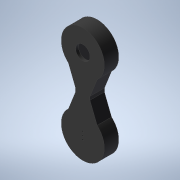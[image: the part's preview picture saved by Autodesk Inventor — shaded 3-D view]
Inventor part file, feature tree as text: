
AUTODESK INVENTOR PART (.ipt)
format: ipt  version: 2022 (Build 260153000, 153)  size: 239,616 bytes
history: native  units: in
note: dims shown in document units (in); Inventor stores cm internally (conversion verified against a paired STEP export)
features: extrude x11, sketch x11, thread x4, chamfer x1
ambient origin geometry x8: Origin, YZ Plane, XZ Plane, XY Plane, X Axis, Y Axis, Z Axis, Center Point
bodies: Solid1 (feature_tree)
feature tree (27):
  extrude  "Extrusion1"  Depth=2.3622in
  extrude  "Extrusion2"  Depth=0.7874in TaperAngle=0.0deg
  extrude  "Extrusion3"  Depth=0.6299in TaperAngle=0.0deg
  extrude  "Extrusion4"  Depth=0.0787in
  extrude  "Extrusion5"  Depth=0.0787in TaperAngle=0.0deg
  extrude  "Extrusion6"  Depth=1.1811in
  thread  "Thread1"  [1 undecoded]
  thread  "Thread2"  [1 undecoded]
  thread  "Thread3"  [1 undecoded]
  thread  "Thread4"  [1 undecoded]
  extrude  "Extrusion7"  Depth=0.2992in
  extrude  "Extrusion8"  Depth=0.1969in
  extrude  "Extrusion9"  Depth=0.1969in
  extrude  "Extrusion10"  Depth=0.3937in TaperAngle=0.0deg
  extrude  "Extrusion11"  Depth=0.0787in
  chamfer  "Chamfer2"  Distance=0.1969in
  sketch  "Sketch1"  dims[d0=2.3622in d1=2.3622in]
  sketch  "Sketch2"  dims[d2=1.5748in d3=0.7874in d4=0.0in]
  sketch  "Sketch3"  dims[d5=0.7874in d6=0.6299in d7=0.0in]
  sketch  "Sketch4"  dims[d11=0.0787in d12=0.0787in]
  sketch  "Sketch5"  dims[d13=0.0787in d14=1.1201in d15=0.0in]
  sketch  "Sketch6"  dims[d16=0.3937in d17=1.1811in d18=0.3937in d19=0.4134in d20=0.6299in d21=0.0in d22=0.2992in]
  sketch  "Sketch7"  dims[d23=0.2992in d24=0.1614in]
  sketch  "Sketch8"  dims[d25=0.1614in d26=0.1969in]
  sketch  "Sketch9"  dims[d27=0.1969in d28=0.1969in]
  sketch  "Sketch10"  dims[d29=0.1969in d30=0.3937in d31=0.0in]
  sketch  "Sketch11"  dims[d32=0.1614in d33=0.1614in d34=0.1969in d35=0.1969in d36=0.1772in d37=0.1772in d38=0.1772in d39=0.1772in d40=0.315in d41=0.0in d42=0.315in d43=0.0in d44=0.315in d45=0.0in d46=0.315in d47=0.0in d48=0.315in d49=0.0in d50=0.7874in d51=0.1575in d52=0.0in d53=0.7874in d54=1.1811in d55=1.1811in d56=2.8425in d57=0.0in d58=0.7874in d59=0.0in d60=0.7874in d61=0.6299in d62=0.0in d63=0.0787in d64=0.0787in d65=0.8701in d66=0.0in d67=0.4724in d68=0.0787in d69=45.0deg]
note: 4 required parameter values undecoded (feature->parameter linkage not recoverable at this tier; creation-order binding heuristic only, values carry confidence <= 0.55)
